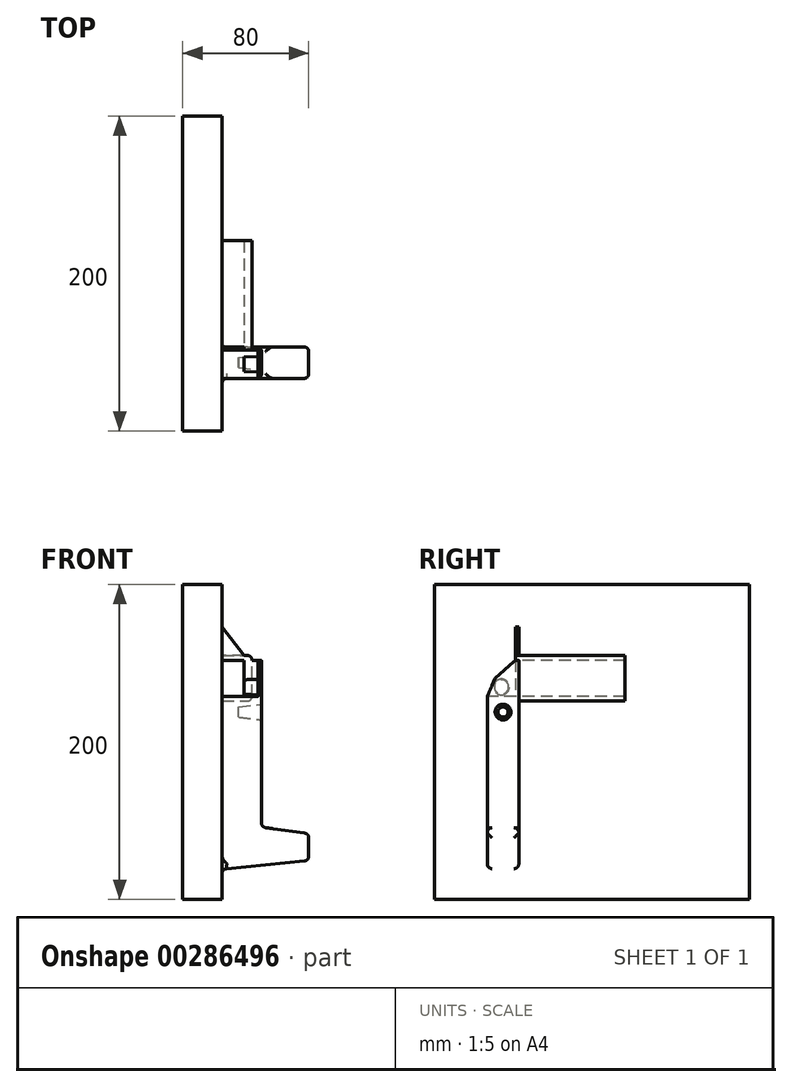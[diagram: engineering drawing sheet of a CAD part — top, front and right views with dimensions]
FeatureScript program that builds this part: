
annotation { "Feature Type Name" : "Feature", "Feature Type Description" : "" }
export const myFeature = defineFeature(function(context is Context, id is Id, definition is map)
    precondition{}
    {
        {
            var Q0;
            Q0=qCreatedBy(makeId("Front.planeOp"),FACE);
            var sketch = newSketch(context, id + "F0", { "sketchPlane" : qUnion([Q0])});
            skLineSegment(sketch, "E0.bottom", {"start": v(0, 0) * mm, "end": v(19, 0) * mm});
            skLineSegment(sketch, "E0.top", {"start": v(0, 29) * mm, "end": v(19, 29) * mm});
            skLineSegment(sketch, "E0.left", {"start": v(0, 0) * mm, "end": v(0, 29) * mm});
            skLineSegment(sketch, "E0.right", {"start": v(19, 0) * mm, "end": v(19, 29) * mm});
            skLineSegment(sketch, "E1.bottom", {"start": v(0, 26) * mm, "end": v(14, 26) * mm});
            skLineSegment(sketch, "E1.top", {"start": v(0, 3) * mm, "end": v(14, 3) * mm});
            skLineSegment(sketch, "E1.left", {"start": v(0, 26) * mm, "end": v(0, 3) * mm});
            skLineSegment(sketch, "E1.right", {"start": v(14, 26) * mm, "end": v(14, 3) * mm});
            skSolve(sketch);
        }
        {
            var Q0;
            {var subQ4=sQuery(id+"F0.wireOp",EDGE,"E0.bottom");Q0=makeQuery(id+"F0.imprint","IMPRINT",FACE,{"disambiguationData":[TD([[makeQuery(id+"F0.imprint","IMPRINT",EDGE,{"derivedFrom":subQ4}),1.0]])]});}
            extrude(context, id + "F1", {"entities" : qUnion([Q0]), "oppositeDirection" : true, "depth" : 69.5 * mm, "offsetDistance" : 25 * mm});
        }
        {
            var Q0;
            Q0=qCreatedBy(makeId("Right.planeOp"),FACE);
            var sketch = newSketch(context, id + "F2", { "sketchPlane" : qUnion([Q0])});
            skLineSegment(sketch, "E2.bottom", {"start": v(148.6, 74.09) * mm, "end": v(-51.4, 74.09) * mm});
            skLineSegment(sketch, "E2.top", {"start": v(148.6, -125.91) * mm, "end": v(-51.4, -125.91) * mm});
            skLineSegment(sketch, "E2.left", {"start": v(148.6, 74.09) * mm, "end": v(148.6, -125.91) * mm});
            skLineSegment(sketch, "E2.right", {"start": v(-51.4, 74.09) * mm, "end": v(-51.4, -125.91) * mm});
            skPoint(sketch, "E2.middle", {"position": v(48.6, -25.91) * mm});
            skSolve(sketch);
        }
        {
            var Q0;
            Q0=qSketchRegion(id+"F2",true);
            extrude(context, id + "F3", {"entities" : qUnion([Q0]), "oppositeDirection" : true, "depth" : 25 * mm, "offsetDistance" : 25 * mm});
        }
        {
            var Q0;
            Q0=makeQuery(id+"F1.opExtrude","SWEPT_FACE",FACE,{"disambiguationData":[OSD([sQuery(id+"F0.wireOp",EDGE,"E1.top")])]});
            var sketch = newSketch(context, id + "F4", { "sketchPlane" : qUnion([Q0])});
            skLineSegment(sketch, "E3.bottom", {"start": v(0, 2) * mm, "end": v(25, 2) * mm});
            skLineSegment(sketch, "E3.top", {"start": v(0, -18) * mm, "end": v(25, -18) * mm});
            skLineSegment(sketch, "E3.left", {"start": v(0, 2) * mm, "end": v(0, -18) * mm});
            skLineSegment(sketch, "E3.right", {"start": v(25, 2) * mm, "end": v(25, -18) * mm});
            skSolve(sketch);
        }
        {
            var Q0;
            Q0=qSketchRegion(id+"F4",true);
            extrude(context, id + "F5", {"entities" : qUnion([Q0]), "operationType" : NewBodyOperationType.ADD, "oppositeDirection" : true, "depth" : 83 * mm, "offsetDistance" : 25 * mm});
        }
        {
            var Q0;
            Q0=makeQuery(id+"F5.boolean.opBoolean","MERGE",FACE,{"derivedFrom":[makeQuery(id+"F1.opExtrude","SWEPT_FACE",FACE,{"disambiguationData":[OSD([sQuery(id+"F0.wireOp",EDGE,"E1.top")])]}),makeQuery(id+"F5.opExtrude","CAP_FACE",FACE,{"disambiguationData":[OSD([sQuery(id+"F4.wireOp",EDGE,"E3.bottom"),sQuery(id+"F4.wireOp",EDGE,"E3.top"),sQuery(id+"F4.wireOp",EDGE,"E3.left"),sQuery(id+"F4.wireOp",EDGE,"E3.right")])],"isStart":true})]});
            var sketch = newSketch(context, id + "F6", { "sketchPlane" : qUnion([Q0])});
            skLineSegment(sketch, "E4", {"start": v(19, 0) * mm, "end": v(22.7, 0) * mm});
            skLineSegment(sketch, "E5", {"start": v(22.7, 0) * mm, "end": v(22.7, -18) * mm});
            skLineSegment(sketch, "E6", {"start": v(22.7, -18) * mm, "end": v(25, -18) * mm});
            skLineSegment(sketch, "E7", {"start": v(25, -18) * mm, "end": v(25, 2) * mm});
            skLineSegment(sketch, "E8", {"start": v(25, 2) * mm, "end": v(19, 2) * mm});
            skLineSegment(sketch, "E9", {"start": v(19, 2) * mm, "end": v(19, 0) * mm});
            skSolve(sketch);
        }
        {
            var Q0;
            Q0=qSketchRegion(id+"F6",true);
            var Q1;
            Q1=makeQuery(id+"F1.opExtrude","SWEPT_FACE",FACE,{"disambiguationData":[OSD([sQuery(id+"F0.wireOp",EDGE,"E1.bottom")])]});
            extrude(context, id + "F7", {"entities" : qUnion([Q0]), "operationType" : NewBodyOperationType.ADD, "endBound" : BoundingType.UP_TO_SURFACE, "depth" : 25 * mm, "endBoundEntityFace" : qUnion([Q1]), "offsetDistance" : 25 * mm});
        }
        {
            var Q0;
            Q0=makeQuery(id+"F7.opExtrude","SWEPT_FACE",FACE,{"disambiguationData":[OSD([sQuery(id+"F6.wireOp",EDGE,"E5")])]});
            var sketch = newSketch(context, id + "F8", { "sketchPlane" : qUnion([Q0])});
            skCircle(sketch, "E10", {"center": v(9, 9) * mm, "radius": 5 * mm});
            skPoint(sketch, "E11", {"position": v(9, 3) * mm});
            skLineSegment(sketch, "E12", {"start": v(0, 26) * mm, "end": v(13.02, 14.4) * mm});
            skLineSegment(sketch, "E13", {"start": v(13.02, 14.4) * mm, "end": v(18, 3) * mm});
            skLineSegment(sketch, "E14", {"start": v(18, 3) * mm, "end": v(18, 26) * mm});
            skLineSegment(sketch, "E15", {"start": v(18, 26) * mm, "end": v(0, 26) * mm});
            skSolve(sketch);
        }
        {
            var Q0;
            Q0=makeQuery(id+"F8.imprint","IMPRINT",FACE,{"disambiguationData":[TD([[makeQuery(id+"F8.imprint","IMPRINT",EDGE,{"derivedFrom":sQuery(id+"F8.wireOp",EDGE,"E12")}),1.0]])]});
            extrude(context, id + "F9", {"entities" : qUnion([Q0]), "operationType" : NewBodyOperationType.REMOVE, "oppositeDirection" : true, "depth" : 25 * mm, "offsetDistance" : 25 * mm});
        }
        {
            var Q0;
            Q0=makeQuery(id+"F8.imprint","IMPRINT",FACE,{"disambiguationData":[TD([[makeQuery(id+"F8.imprint","IMPRINT",EDGE,{"derivedFrom":sQuery(id+"F8.wireOp",EDGE,"E10")}),1.0]])]});
            var Q1;
            Q1=makeQuery(id+"F1.opExtrude","SWEPT_FACE",FACE,{"disambiguationData":[OSD([sQuery(id+"F0.wireOp",EDGE,"E1.right")])]});
            extrude(context, id + "F10", {"entities" : qUnion([Q0]), "operationType" : NewBodyOperationType.ADD, "endBound" : BoundingType.UP_TO_SURFACE, "depth" : 25 * mm, "endBoundEntityFace" : qUnion([Q1]), "offsetDistance" : 25 * mm, "hasDraft" : true, "draftAngle" : 3 * degree, "draftPullDirection" : true});
        }
        {
            var Q0;
            Q0=makeQuery(id+"F7.boolean.opBoolean","MERGE",FACE,{"derivedFrom":[makeQuery(id+"F1.opExtrude","CAP_FACE",FACE,{"disambiguationData":[OSD([sQuery(id+"F0.wireOp",EDGE,"E0.bottom"),sQuery(id+"F0.wireOp",EDGE,"E0.top"),sQuery(id+"F0.wireOp",EDGE,"E0.left"),sQuery(id+"F0.wireOp",EDGE,"E0.right"),sQuery(id+"F0.wireOp",EDGE,"E1.bottom"),sQuery(id+"F0.wireOp",EDGE,"E1.top"),sQuery(id+"F0.wireOp",EDGE,"E1.right")])],"isStart":true}),makeQuery(id+"F7.opExtrude","SWEPT_FACE",FACE,{"disambiguationData":[OSD([sQuery(id+"F6.wireOp",EDGE,"E4")])]})]});
            var sketch = newSketch(context, id + "F11", { "sketchPlane" : qUnion([Q0])});
            skLineSegment(sketch, "E16", {"start": v(14, 29) * mm, "end": v(0, 47.23) * mm});
            skLineSegment(sketch, "E17", {"start": v(0, 47.23) * mm, "end": v(0, 29) * mm});
            skLineSegment(sketch, "E18", {"start": v(0, 29) * mm, "end": v(14, 29) * mm});
            skSolve(sketch);
        }
        {
            var Q0;
            Q0=qSketchRegion(id+"F11",true);
            var Q1;
            Q1=makeQuery(id+"F7.boolean.opBoolean","MERGE",FACE,{"derivedFrom":[makeQuery(id+"F5.opExtrude","SWEPT_FACE",FACE,{"disambiguationData":[OSD([sQuery(id+"F4.wireOp",EDGE,"E3.bottom")])]}),makeQuery(id+"F7.opExtrude","SWEPT_FACE",FACE,{"disambiguationData":[OSD([sQuery(id+"F6.wireOp",EDGE,"E8")])]})]});
            extrude(context, id + "F12", {"entities" : qUnion([Q0]), "operationType" : NewBodyOperationType.ADD, "endBound" : BoundingType.UP_TO_SURFACE, "oppositeDirection" : true, "depth" : 25 * mm, "endBoundEntityFace" : qUnion([Q1]), "offsetDistance" : 25 * mm});
        }
        {
            var Q0;
            Q0=makeQuery(id+"F7.boolean.opBoolean","MERGE",FACE,{"derivedFrom":[makeQuery(id+"F5.opExtrude","SWEPT_FACE",FACE,{"disambiguationData":[OSD([sQuery(id+"F4.wireOp",EDGE,"E3.top")])]}),makeQuery(id+"F7.opExtrude","SWEPT_FACE",FACE,{"disambiguationData":[OSD([sQuery(id+"F6.wireOp",EDGE,"E6")])]})]});
            var sketch = newSketch(context, id + "F13", { "sketchPlane" : qUnion([Q0])});
            skLineSegment(sketch, "E19", {"start": v(25, -80) * mm, "end": v(55, -84.18) * mm});
            skLineSegment(sketch, "E20", {"start": v(55, -84.18) * mm, "end": v(55, -101.35) * mm});
            skLineSegment(sketch, "E21", {"start": v(55, -101.35) * mm, "end": v(0, -106.69) * mm});
            skLineSegment(sketch, "E22", {"start": v(0, -106.69) * mm, "end": v(0, -80) * mm});
            skLineSegment(sketch, "E23", {"start": v(0, -80) * mm, "end": v(25, -80) * mm});
            skSolve(sketch);
        }
        {
            var Q0;
            Q0=qSketchRegion(id+"F13",true);
            var Q1;
            Q1=makeQuery(id+"F7.boolean.opBoolean","MERGE",FACE,{"derivedFrom":[makeQuery(id+"F5.opExtrude","SWEPT_FACE",FACE,{"disambiguationData":[OSD([sQuery(id+"F4.wireOp",EDGE,"E3.bottom")])]}),makeQuery(id+"F7.opExtrude","SWEPT_FACE",FACE,{"disambiguationData":[OSD([sQuery(id+"F6.wireOp",EDGE,"E8")])]})]});
            extrude(context, id + "F14", {"entities" : qUnion([Q0]), "operationType" : NewBodyOperationType.ADD, "endBound" : BoundingType.UP_TO_SURFACE, "oppositeDirection" : true, "depth" : 25 * mm, "endBoundEntityFace" : qUnion([Q1]), "offsetDistance" : 25 * mm});
        }
        {
            var Q0;
            Q0=makeQuery(id+"F7.boolean.opBoolean","MERGE",FACE,{"derivedFrom":[makeQuery(id+"F5.opExtrude","SWEPT_FACE",FACE,{"disambiguationData":[OSD([sQuery(id+"F4.wireOp",EDGE,"E3.right")])]}),makeQuery(id+"F7.opExtrude","SWEPT_FACE",FACE,{"disambiguationData":[OSD([sQuery(id+"F6.wireOp",EDGE,"E7")])]})]});
            var sketch = newSketch(context, id + "F15", { "sketchPlane" : qUnion([Q0])});
            skCircle(sketch, "E24", {"center": v(-8, -6.95) * mm, "radius": 5 * mm});
            skPoint(sketch, "E24.centerSnap0", {"position": v(-8, -80) * mm});
            skSolve(sketch);
        }
        {
            var Q0;
            Q0 = qSketchRegion(id + "F15", true);
            extrude(context, id + "F16", {"entities" : qUnion([Q0]), "operationType" : NewBodyOperationType.REMOVE, "oppositeDirection" : true, "depth" : 14.5 * mm, "offsetDistance" : 25 * mm, "hasDraft" : true, "draftAngle" : 7 * degree, "draftPullDirection" : true});
        }
        {
            var Q0;
            Q0=makeQuery(id+"F7.boolean.opBoolean","MERGE",EDGE,{"derivedFrom":[makeQuery(id+"F5.opExtrude","SWEPT_EDGE",EDGE,{"disambiguationData":[OSD([sQuery(id+"F4.wireOp",EDGE,"E3.bottom"),sQuery(id+"F4.wireOp",EDGE,"E3.right")])]}),makeQuery(id+"F7.opExtrude","SWEPT_EDGE",EDGE,{"disambiguationData":[OSD([sQuery(id+"F6.wireOp",EDGE,"E7"),sQuery(id+"F6.wireOp",EDGE,"E8")])]})]});
            var Q1;
            Q1=makeQuery(id+"F7.boolean.opBoolean","MERGE",EDGE,{"derivedFrom":[makeQuery(id+"F5.opExtrude","SWEPT_EDGE",EDGE,{"disambiguationData":[OSD([sQuery(id+"F4.wireOp",EDGE,"E3.top"),sQuery(id+"F4.wireOp",EDGE,"E3.right")])]}),makeQuery(id+"F7.opExtrude","SWEPT_EDGE",EDGE,{"disambiguationData":[OSD([sQuery(id+"F6.wireOp",EDGE,"E6"),sQuery(id+"F6.wireOp",EDGE,"E7")])]})]});
            var Q2;
            {var subQ0=sQuery(id+"F4.wireOp",EDGE,"E3.right");Q2=makeQuery(id+"F14.boolean.opBoolean","MERGE",EDGE,{"derivedFrom":[makeQuery(id+"F5.opExtrude","CAP_EDGE",EDGE,{"disambiguationData":[OSD([subQ0])],"isStart":false}),makeQuery(id+"F14.opExtrude","SWEPT_EDGE",EDGE,{"disambiguationData":[OSD([sQuery(id+"F4.wireOp",EDGE,"E3.top"),subQ0,sQuery(id+"F6.wireOp",EDGE,"E6"),sQuery(id+"F6.wireOp",EDGE,"E7"),sQuery(id+"F13.wireOp",EDGE,"E19"),sQuery(id+"F13.wireOp",EDGE,"E23")])]})]});}
            var Q3;
            Q3=makeQuery(id+"F14.opExtrude","SWEPT_FACE",FACE,{"disambiguationData":[OSD([sQuery(id+"F13.wireOp",EDGE,"E20")])]});
            var Q4;
            Q4=makeQuery(id+"F14.opExtrude","SWEPT_FACE",FACE,{"disambiguationData":[OSD([sQuery(id+"F13.wireOp",EDGE,"E21")])]});
            var Q5;
            Q5=makeQuery(id+"F1.opExtrude","SWEPT_EDGE",EDGE,{"disambiguationData":[OSD([sQuery(id+"F0.wireOp",EDGE,"E0.bottom"),sQuery(id+"F0.wireOp",EDGE,"E0.right")])]});
            var Q6;
            Q6=makeQuery(id+"F1.opExtrude","SWEPT_EDGE",EDGE,{"disambiguationData":[OSD([sQuery(id+"F0.wireOp",EDGE,"E0.top"),sQuery(id+"F0.wireOp",EDGE,"E0.right")])]});
            fillet(context, id + "F17", {"entities" : qUnion([Q0, Q1, Q2, Q3, Q4, Q5, Q6]), "radius" : 3 * mm, "tangentPropagation" : true, "allowEdgeOverflow" : false});
        }
    });
